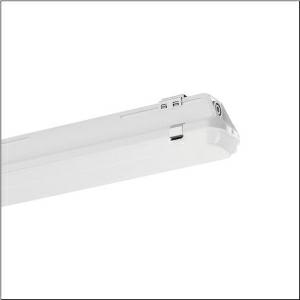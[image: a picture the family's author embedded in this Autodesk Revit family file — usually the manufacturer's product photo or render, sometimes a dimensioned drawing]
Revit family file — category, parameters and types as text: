
# Revit family: monsun_r__21_emergency_51fb107p467c3g_1234
name_source: partatom
category: Lighting Fixtures
units: mm (PartAtom-declared; Revit-internal decimal feet)

## family parameters
Cut with Voids When Loaded = No
Host = Face
Light Source = No
Part Type = Normal
Room Calculation Point = No
Round Connector Dimension = Use Diameter
Shared = No

## types (1)
- --- (1 x LED, 910 lm, 7.1 W, 4000K)
    Apparent Load = 7 VA
    CIE Flux Codes = 47 77 93 94 100
    Color Rendering = 80
    Color Temperature = 4000K
    Default Elevation = 1800 mm
    Description = Monsun® 21 emergency, damp-proof luminaire, chain hanger, primary optical cover: enclosure, of PMMA, light emission: direct distribution, primary light characteristic: symmetric, installation type: suspended mounting, surface-mounted, horizontal mounting, vertical mounting, LED, rated luminous flux: 6.060lm, luminous efficacy: 178lm/W, light colour: 840, colour temperature: 4000K, control gear: ON/OFF, with terminal, 4-pole, max. 2.5mm², mains connection: 220..240V, AC, 50/60Hz, rated input power: 38W, control gear: single battery element, battery: LiFePO4, 9Ah, housing, of glass-fibre reinforced polyester, uncoated, bright grey, incl. chain hanger, length: 1.590mm, width: 90mm, height: 88mm, clip for enclosure, of stainless steel (V2A), ceiling mounting element, of stainless steel (V2A), chain hanger, of stainless steel (V2A), protection rating (complete): IP66, insulation class (complete): insulation class I (protective earthing), certification: CE, UKCA, protection symbol: D, impact resistance: IK04, permissible operating ambient temperature: +5..+25°C, standard: EN 50419, EN 60598-2-1, EN 60598-2-22, corresponds to IFS (International Featured Standards) requirements for safety and quality in the food industry, for indoor or canopied outdoor use, no direct snow, no direct sun, no direct rain, LABS conformity tested according to VDMA 24364:2018-05, contact your sales advisor before using the luminaires in applications with unclear chemical exposure, large temperature fluctuations or condensation-forming humidity, packaging unit: 1 piece
    Height = 89 mm
    Lamp = 1 x LED
    Lamp Light Flux = 910 lm
    Lamp Power = 7.1 W
    Lamp count = 1
    Length = 1590 mm
    Luminous efficacy = 128 lm/W
    Manufacturer = Siteco
    ModVariant = No
    Model = 51FB107P467C3G
    Mounting Place = Ceiling
    Mounting Type = Surface mounted
    Number of Poles = 1
    OnlyDefault = Yes
    Power Factor = 1
    Product Name = Monsun® 21 emergency
    Product group = damp-proof luminaire
    ProductGroupID = 300
    Protection Class = Protection class I
    Protection Degree = IP 66
    RLX_Detail_Level = 1
    RLX_Emergency_Light_Flux = 0 lm
    RLX_Emergency_Type = 0
    RLX_Emergency_Type_DB = No
    RlxData = <blob elided: 89049 chars, md5=214dc79f>
    Socket = socket
    Standby Power = 0 W
    System Light Flux = 910 lm
    System Power = 7 W
    Type Comments = : emergency light operation: 3 h
    Type Image = l_1319656.jpg
    URL = http://relux.com
    VarID = @adj_031770
    Voltage = 0 V
    Weight = 0.00 kg
    Width = 90 mm

## geometry (parser evidence)
native form markers: Blend x4, Sweep x13
no freeform markers — native parametric forms only
